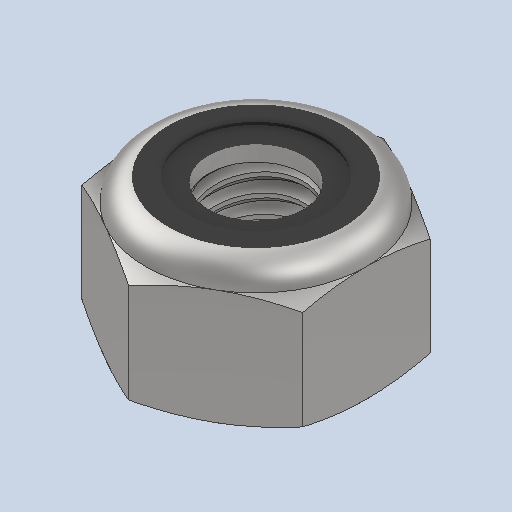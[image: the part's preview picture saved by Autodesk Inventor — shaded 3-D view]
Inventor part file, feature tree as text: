
AUTODESK INVENTOR PART (.ipt)
format: ipt  version: 2024 (Build 280153000, 153)  size: 462,848 bytes
history: native  units: in
note: dims shown in document units (in); Inventor stores cm internally (conversion verified against a paired STEP export)
features: other x1, revolve x1
ambient origin geometry x8: Origin, YZ Plane, XZ Plane, XY Plane, X Axis, Y Axis, Z Axis, Center Point
bodies: Solid1 (feature_tree), Solid2 (feature_tree)
feature tree (2):
  other  "Cut-Revolve4"
  revolve  "Revolve2"  [1 undecoded]
note: 1 required parameter value undecoded (feature->parameter linkage not recoverable at this tier; creation-order binding heuristic only, values carry confidence <= 0.55)
